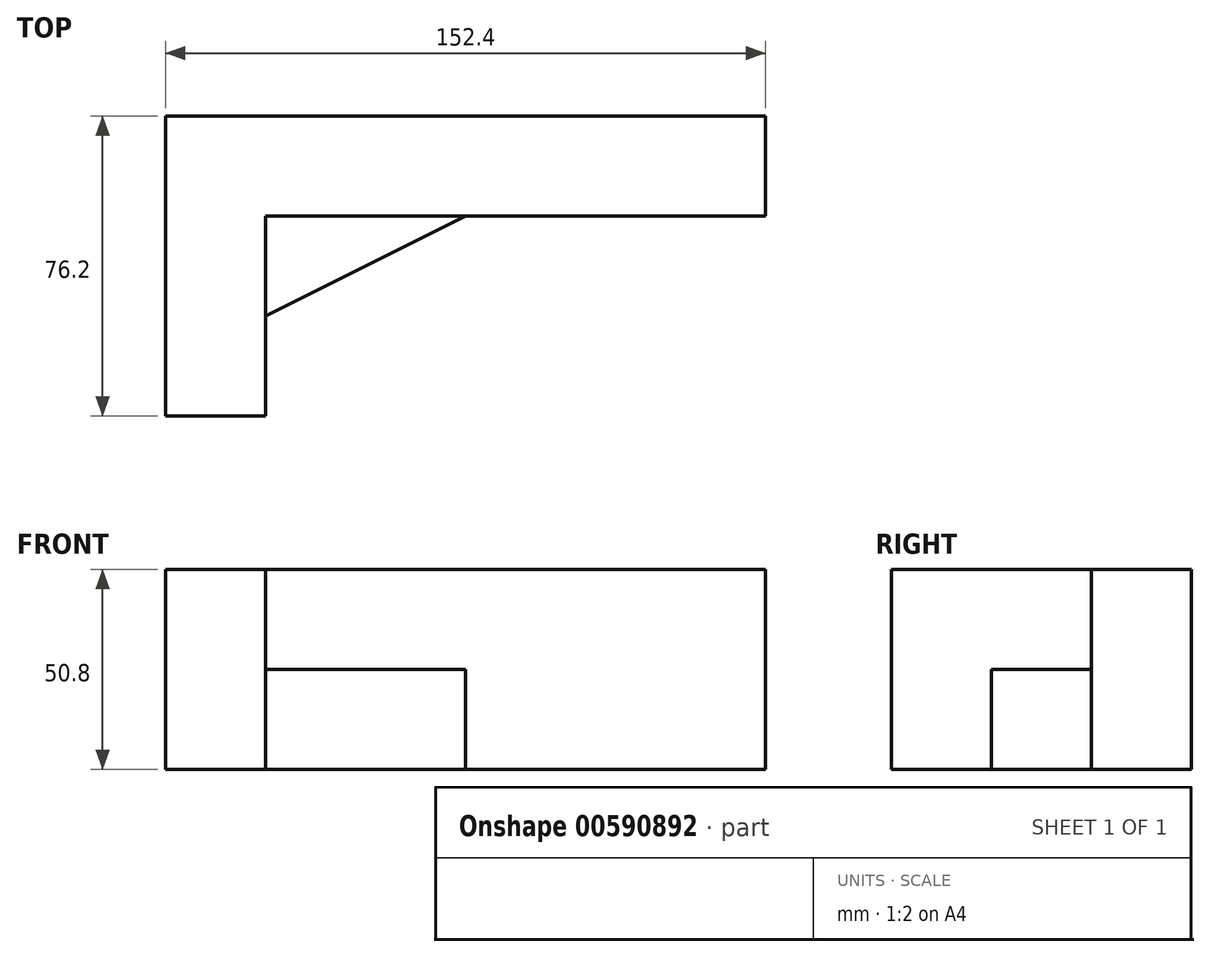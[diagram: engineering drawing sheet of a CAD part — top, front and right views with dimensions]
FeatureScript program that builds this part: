
annotation { "Feature Type Name" : "Feature", "Feature Type Description" : "" }
export const myFeature = defineFeature(function(context is Context, id is Id, definition is map)
    precondition{}
    {
        {
            var Q0;
            Q0=qCreatedBy(makeId("Front.planeOp"),FACE);
            var sketch = newSketch(context, id + "F0", { "sketchPlane" : qUnion([Q0])});
            skLineSegment(sketch, "E0.bottom", {"start": v(0, 0) * mm, "end": v(152.4, 0) * mm});
            skLineSegment(sketch, "E0.top", {"start": v(0, 50.8) * mm, "end": v(152.4, 50.8) * mm});
            skLineSegment(sketch, "E0.left", {"start": v(0, 0) * mm, "end": v(0, 50.8) * mm});
            skLineSegment(sketch, "E0.right", {"start": v(152.4, 0) * mm, "end": v(152.4, 50.8) * mm});
            skSolve(sketch);
        }
        {
            var Q0;
            Q0=makeQuery(id+"F0.imprint","IMPRINT",FACE,{"disambiguationData":[TD([[makeQuery(id+"F0.imprint","IMPRINT",EDGE,{"derivedFrom":sQuery(id+"F0.wireOp",EDGE,"E0.bottom")}),1.0]])]});
            extrude(context, id + "F1", {"entities" : qUnion([Q0]), "oppositeDirection" : true, "depth" : 76.2 * mm, "offsetDistance" : 25.4 * mm});
        }
        {
            var Q0;
            Q0=makeQuery(id+"F1.opExtrude","SWEPT_FACE",FACE,{"disambiguationData":[OSD([sQuery(id+"F0.wireOp",EDGE,"E0.top")])]});
            var sketch = newSketch(context, id + "F2", { "sketchPlane" : qUnion([Q0])});
            skLineSegment(sketch, "E1", {"start": v(0, 0) * mm, "end": v(25.4, 0) * mm});
            skLineSegment(sketch, "E2", {"start": v(25.4, 0) * mm, "end": v(25.4, 50.8) * mm});
            skLineSegment(sketch, "E3", {"start": v(25.4, 50.8) * mm, "end": v(152.4, 50.8) * mm});
            skLineSegment(sketch, "E4", {"start": v(152.4, 50.8) * mm, "end": v(152.4, 76.2) * mm});
            skLineSegment(sketch, "E5", {"start": v(152.4, 76.2) * mm, "end": v(0, 76.2) * mm});
            skLineSegment(sketch, "E6", {"start": v(0, 76.2) * mm, "end": v(0, 0) * mm});
            skSolve(sketch);
        }
        {
            var Q0;
            {var subQ0=sQuery(id+"F2.wireOp",EDGE,"E2");Q0=makeQuery(id+"F2.imprint","IMPRINT",FACE,{"disambiguationData":[TD([[makeQuery(id+"F2.imprint","IMPRINT",EDGE,{"derivedFrom":subQ0}),-1.0]])]});}
            extrude(context, id + "F3", {"entities" : qUnion([Q0]), "operationType" : NewBodyOperationType.REMOVE, "oppositeDirection" : true, "depth" : 50.8 * mm, "offsetDistance" : 25.4 * mm});
        }
        {
            var Q0;
            Q0=makeQuery(id+"F1.opExtrude","SWEPT_FACE",FACE,{"disambiguationData":[OSD([sQuery(id+"F0.wireOp",EDGE,"E0.bottom")])]});
            var sketch = newSketch(context, id + "F4", { "sketchPlane" : qUnion([Q0])});
            skLineSegment(sketch, "E7", {"start": v(25.4, -50.8) * mm, "end": v(25.4, -25.4) * mm});
            skLineSegment(sketch, "E8", {"start": v(25.4, -25.4) * mm, "end": v(76.2, -50.8) * mm});
            skLineSegment(sketch, "E9", {"start": v(76.2, -50.8) * mm, "end": v(25.4, -50.8) * mm});
            skSolve(sketch);
        }
        {
            var Q0;
            Q0=makeQuery(id+"F4.imprint","IMPRINT",FACE,{"disambiguationData":[TD([[makeQuery(id+"F4.imprint","IMPRINT",EDGE,{"derivedFrom":sQuery(id+"F4.wireOp",EDGE,"E7")}),1.0]])]});
            extrude(context, id + "F5", {"entities" : qUnion([Q0]), "oppositeDirection" : true, "depth" : 25.4 * mm, "offsetDistance" : 25.4 * mm});
        }
    });
